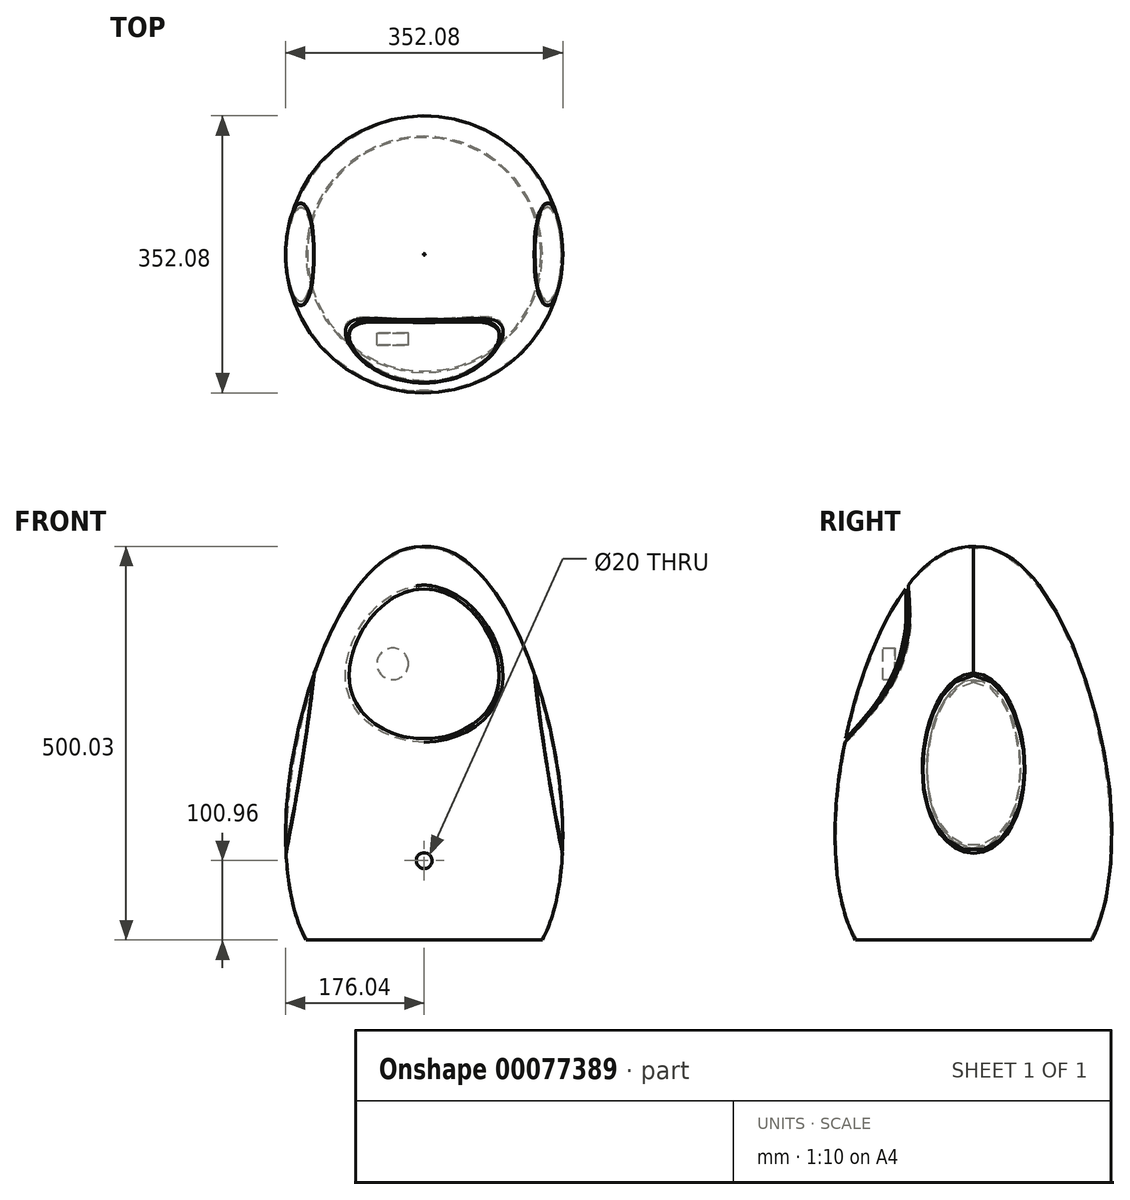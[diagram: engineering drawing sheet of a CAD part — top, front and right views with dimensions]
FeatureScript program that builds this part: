
annotation { "Feature Type Name" : "Feature", "Feature Type Description" : "" }
export const myFeature = defineFeature(function(context is Context, id is Id, definition is map)
    precondition{}
    {
        {
            var Q0;
            Q0=qCreatedBy(makeId("Front.planeOp"),FACE);
            var sketch = newSketch(context, id + "F0", { "sketchPlane" : qUnion([Q0])});
            skArc(sketch, "E0", {"start": v(0, -150) * mm, "mid": v(150, 0) * mm, "end": v(0, 150) * mm});
            skLineSegment(sketch, "E1", {"start": v(0, 150) * mm, "end": v(0, -150) * mm, "construction": true});
            skSolve(sketch);
        }
        {
            var Q0;
            Q0=sQuery(id+"F0.wireOp",EDGE,"E0");
            var Q1;
            Q1=sQuery(id+"F0.wireOp",EDGE,"E1");
            revolve(context, id + "F1", {"bodyType" : ToolBodyType.SURFACE, "surfaceEntities" : qUnion([Q0]), "axis" : qUnion([Q1]), "revolveType" : RevolveType.ONE_DIRECTION, "angle" : 360 * degree});
        }
        {
            var Q0;
            Q0=qCreatedBy(makeId("Front.planeOp"),FACE);
            var sketch = newSketch(context, id + "F2", { "sketchPlane" : qUnion([Q0])});
            skFitSpline(sketch, "E2", {"points": [v(1, 449.04) * mm, v(162.92, 203.43) * mm, v(150, -50.96) * mm], "startDerivative": vector(458.16, 11.78) * mm, "endDerivative": vector(-172.52, -317.15) * mm});
            skFitSpline(sketch, "E3.0", {"points": [v(1.05, 447.04) * mm, v(5.69, 447.16) * mm, v(14.81, 446.46) * mm, v(28.08, 442.76) * mm, v(40.93, 436.58) * mm, v(57.5, 425.25) * mm, v(77.03, 405.76) * mm, v(98.38, 375.34) * mm, v(117.4, 339.48) * mm, v(131.17, 306.37) * mm, v(140.86, 278.75) * mm, v(147.44, 257.65) * mm, v(153.31, 236.38) * mm, v(157.6, 218.67) * mm, v(160.66, 204.6) * mm, v(163.47, 190.65) * mm, v(166.52, 173.43) * mm, v(169.44, 153.16) * mm, v(172.38, 126.74) * mm, v(174.3, 94.99) * mm, v(173.94, 59.3) * mm, v(171.05, 26.48) * mm, v(165.76, -3.1) * mm, v(158.22, -28.98) * mm, v(151.78, -43.5) * mm, v(148.24, -50) * mm]});
            skLineSegment(sketch, "E4", {"start": v(1, 449.04) * mm, "end": v(1.05, 447.04) * mm});
            skLineSegment(sketch, "E5", {"start": v(148.24, -50) * mm, "end": v(150, -50.96) * mm});
            skLineSegment(sketch, "E6", {"start": v(0, 0) * mm, "end": v(0, 281.36) * mm, "construction": true});
            skSolve(sketch);
        }
        {
            var Q0;
            Q0=qCreatedBy(makeId("Front.planeOp"),FACE);
            cPlane(context, id + "F3", {"entities" : qUnion([Q0]), "cplaneType" : CPlaneType.OFFSET, "offset" : 100 * mm, "width" : 150 * mm, "height" : 150 * mm});
        }
        {
            var Q0;
            Q0=makeQuery(id+"F2.imprint","IMPRINT",FACE,{"disambiguationData":[TD([[makeQuery(id+"F2.imprint","IMPRINT",EDGE,{"derivedFrom":sQuery(id+"F2.wireOp",EDGE,"E2")}),-1.0]])]});
            var Q1;
            Q1=sQuery(id+"F2.wireOp",EDGE,"E6");
            revolve(context, id + "F4", {"entities" : qUnion([Q0]), "axis" : qUnion([Q1]), "revolveType" : RevolveType.ONE_DIRECTION, "oppositeDirection" : true, "angle" : 360 * degree});
        }
        {
            var Q0;
            Q0=qCreatedBy(makeId("Front.planeOp"),FACE);
            var sketch = newSketch(context, id + "F5", { "sketchPlane" : qUnion([Q0])});
            skLineSegment(sketch, "E7", {"start": v(0, 0) * mm, "end": v(0, 648.43) * mm, "construction": true});
            skFitSpline(sketch, "E8", {"points": [v(0, 400) * mm, v(-100, 280) * mm, v(0, 200) * mm], "startDerivative": vector(-337.34, -9.76) * mm, "endDerivative": vector(348.63, -14.37) * mm});
            skFitSpline(sketch, "E9.MirrorCS", {"points": [v(0, 400) * mm, v(100, 280) * mm, v(0, 200) * mm], "startDerivative": vector(337.34, -9.76) * mm, "endDerivative": vector(-348.63, -14.37) * mm});
            skFitSpline(sketch, "E10.0", {"points": [v(0.14, 395) * mm, v(-6.44, 394.81) * mm, v(-19.2, 392.68) * mm, v(-37.02, 384.96) * mm, v(-53.17, 373.42) * mm, v(-67.28, 358.83) * mm, v(-78.95, 342.01) * mm, v(-86.33, 326.86) * mm, v(-90.66, 314.5) * mm, v(-93.08, 305.23) * mm, v(-94.64, 296.06) * mm, v(-95.19, 288.6) * mm, v(-95.17, 282.81) * mm, v(-94.83, 277.15) * mm, v(-93.83, 270.3) * mm, v(-91.74, 262.48) * mm, v(-87.81, 252.57) * mm, v(-80.87, 241.2) * mm, v(-69.54, 229.36) * mm, v(-55.48, 219.53) * mm, v(-33.5, 209.41) * mm, v(-13.84, 205.57) * mm, v(0.2, 205) * mm]});
            skFitSpline(sketch, "E11.0", {"points": [v(-0.14, 395) * mm, v(6.44, 394.81) * mm, v(19.2, 392.68) * mm, v(37.02, 384.96) * mm, v(53.17, 373.42) * mm, v(67.28, 358.83) * mm, v(78.95, 342.01) * mm, v(86.33, 326.86) * mm, v(90.66, 314.5) * mm, v(93.08, 305.23) * mm, v(94.64, 296.06) * mm, v(95.19, 288.6) * mm, v(95.17, 282.81) * mm, v(94.83, 277.15) * mm, v(93.83, 270.3) * mm, v(91.74, 262.48) * mm, v(87.81, 252.57) * mm, v(80.87, 241.2) * mm, v(69.54, 229.36) * mm, v(55.48, 219.53) * mm, v(33.5, 209.41) * mm, v(13.84, 205.57) * mm, v(-0.2, 205) * mm]});
            skSolve(sketch);
        }
        {
            var Q0;
            Q0 = qSketchRegion(id + "F5", true);
            extrude(context, id + "F6", {"entities" : qUnion([Q0]), "operationType" : NewBodyOperationType.REMOVE, "endBound" : BoundingType.THROUGH_ALL, "depth" : 25 * mm});
        }
        {
            var Q0;
            Q0=qCreatedBy(id+"F3.planeOp",FACE);
            var sketch = newSketch(context, id + "F7", { "sketchPlane" : qUnion([Q0])});
            skLineSegment(sketch, "E12", {"start": v(0, 214.33) * mm, "end": v(0, 353.6) * mm, "construction": true});
            skLineSegment(sketch, "E13", {"start": v(-40, 300) * mm, "end": v(41.8, 300) * mm, "construction": true});
            skCircle(sketch, "E14", {"center": v(-40, 300) * mm, "radius": 20 * mm});
            skCircle(sketch, "E15.MirrorC", {"center": v(40, 300) * mm, "radius": 20 * mm});
            skSolve(sketch);
        }
        {
            var Q0;
            Q0=makeQuery(id+"F7.imprint","IMPRINT",FACE,{"disambiguationData":[TD([[makeQuery(id+"F7.imprint","IMPRINT",EDGE,{"derivedFrom":sQuery(id+"F7.wireOp",EDGE,"E14")}),1.0]])]});
            var Q1;
            Q1=makeQuery(id+"F7.imprint","IMPRINT",FACE,{"disambiguationData":[TD([[makeQuery(id+"F7.imprint","IMPRINT",EDGE,{"derivedFrom":sQuery(id+"F7.wireOp",EDGE,"E15.MirrorC")}),-1.0]])]});
            extrude(context, id + "F8", {"entities" : qUnion([Q0, Q1]), "depth" : 15 * mm});
        }
        {
            var Q0;
            Q0=qCreatedBy(makeId("Front.planeOp"),FACE);
            var sketch = newSketch(context, id + "F9", { "sketchPlane" : qUnion([Q0])});
            skLineSegment(sketch, "E16", {"start": v(0, 0) * mm, "end": v(0, 181.26) * mm, "construction": true});
            skFitSpline(sketch, "E17", {"points": [v(136.25, 324.64) * mm, v(182.05, 26.05) * mm], "startDerivative": vector(13.21, -182.32) * mm, "endDerivative": vector(74.96, -372.11) * mm});
            skFitSpline(sketch, "E18.0", {"points": [v(137.24, 324.7) * mm, v(138.34, 309.54) * mm, v(142.04, 272.55) * mm, v(155.02, 177.4) * mm, v(170.54, 88.25) * mm, v(183.03, 26.25) * mm]});
            skLineSegment(sketch, "E19", {"start": v(136.25, 324.64) * mm, "end": v(137.24, 324.7) * mm});
            skLineSegment(sketch, "E20", {"start": v(182.05, 26.05) * mm, "end": v(183.03, 26.25) * mm});
            skFitSpline(sketch, "E21.MirrorCS", {"points": [v(-136.25, 324.64) * mm, v(-182.05, 26.05) * mm], "startDerivative": vector(-13.21, -182.32) * mm, "endDerivative": vector(-74.96, -372.11) * mm});
            skLineSegment(sketch, "E22.MirrorCS", {"start": v(-182.05, 26.05) * mm, "end": v(-183.03, 26.25) * mm});
            skLineSegment(sketch, "E23.MirrorCS", {"start": v(-136.25, 324.64) * mm, "end": v(-137.24, 324.7) * mm});
            skFitSpline(sketch, "E24.0", {"points": [v(-137.24, 324.7) * mm, v(-138.34, 309.54) * mm, v(-142.04, 272.55) * mm, v(-155.02, 177.4) * mm, v(-170.54, 88.25) * mm, v(-183.03, 26.25) * mm]});
            skSolve(sketch);
        }
        {
            var Q0;
            Q0 = qSketchRegion(id + "F9", true);
            extrude(context, id + "F10", {"entities" : qUnion([Q0]), "operationType" : NewBodyOperationType.REMOVE, "endBound" : BoundingType.THROUGH_ALL, "oppositeDirection" : true, "depth" : 25 * mm, "hasSecondDirection" : true, "secondDirectionBound" : SecondDirectionBoundingType.THROUGH_ALL, "secondDirectionOppositeDirection" : false, "secondDirectionDepth" : 25 * mm});
        }
        {
            var Q0;
            Q0=qCreatedBy(makeId("Front.planeOp"),FACE);
            cPlane(context, id + "F11", {"entities" : qUnion([Q0]), "cplaneType" : CPlaneType.OFFSET, "offset" : 200 * mm, "width" : 150 * mm, "height" : 150 * mm});
        }
        {
            var Q0;
            Q0 = qSketchRegion(id + "F9", true);
            extrude(context, id + "F12", {"entities" : qUnion([Q0]), "operationType" : NewBodyOperationType.REMOVE, "endBound" : BoundingType.THROUGH_ALL, "oppositeDirection" : true, "depth" : 25 * mm, "hasSecondDirection" : true, "secondDirectionBound" : SecondDirectionBoundingType.THROUGH_ALL, "secondDirectionOppositeDirection" : false, "secondDirectionDepth" : 25 * mm});
        }
        {
            var Q0;
            Q0=qCreatedBy(id+"F11.planeOp",FACE);
            var sketch = newSketch(context, id + "F13", { "sketchPlane" : qUnion([Q0])});
            skCircle(sketch, "E25", {"center": v(0, 50) * mm, "radius": 10 * mm});
            skSolve(sketch);
        }
        {
            var Q0;
            Q0 = qSketchRegion(id + "F13", true);
            extrude(context, id + "F14", {"entities" : qUnion([Q0]), "operationType" : NewBodyOperationType.REMOVE, "oppositeDirection" : true, "depth" : 100 * mm});
        }
        {
            var Q0;
            Q0=qCreatedBy(makeId("Top.planeOp"),FACE);
            cPlane(context, id + "F15", {"entities" : qUnion([Q0]), "cplaneType" : CPlaneType.OFFSET, "offset" : 100 * mm, "oppositeDirection" : true, "width" : 150 * mm, "height" : 150 * mm});
        }
    });
